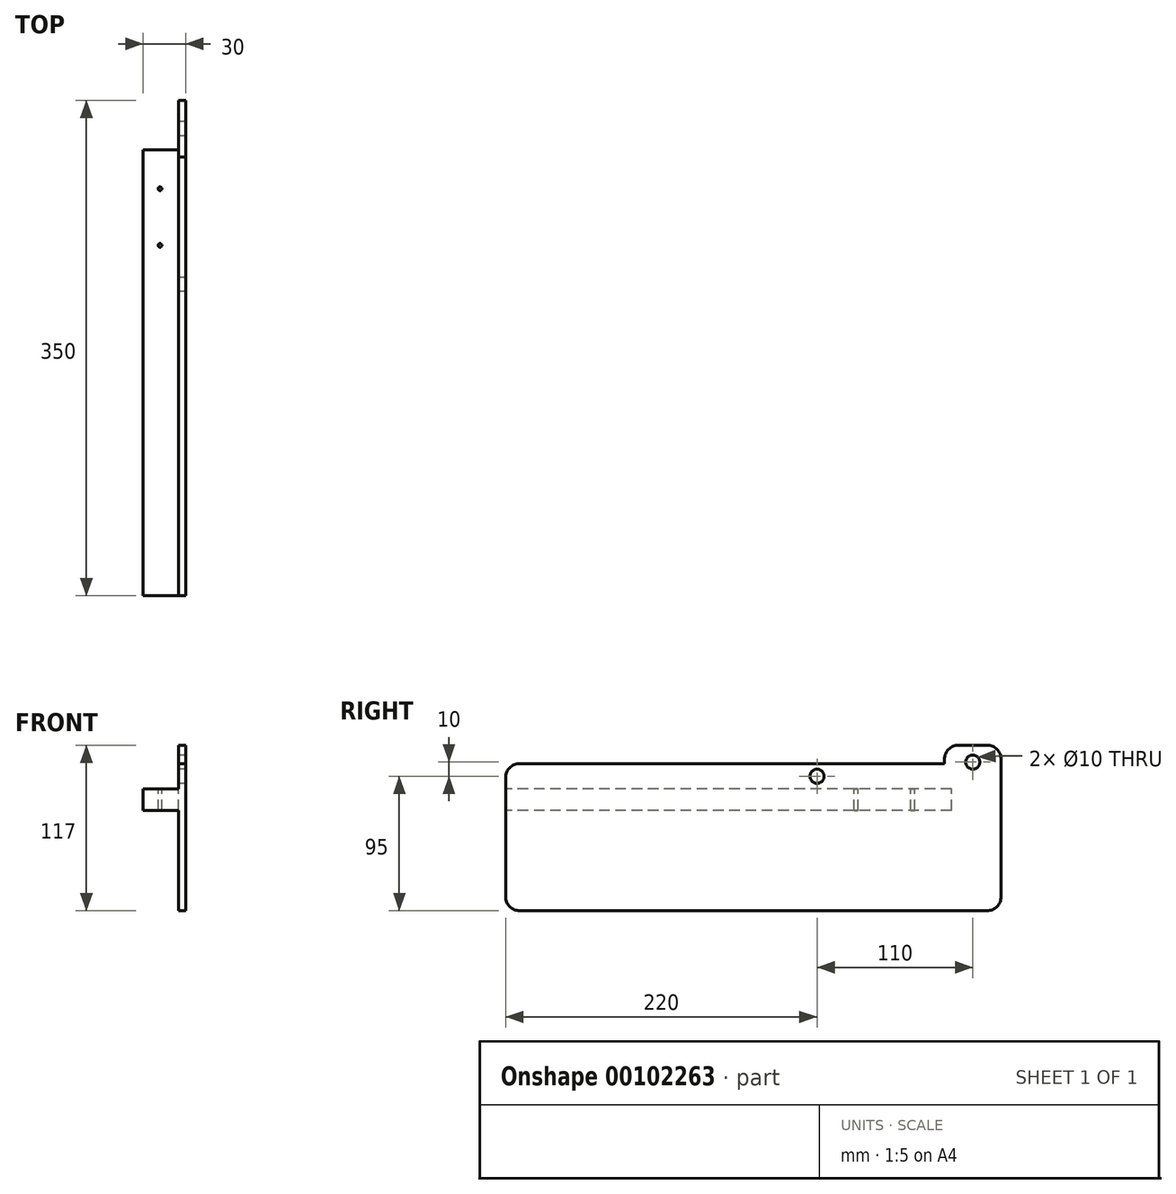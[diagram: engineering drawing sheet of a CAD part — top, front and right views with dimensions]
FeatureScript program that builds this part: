
annotation { "Feature Type Name" : "Feature", "Feature Type Description" : "" }
export const myFeature = defineFeature(function(context is Context, id is Id, definition is map)
    precondition{}
    {
        {
            var Q0;
            Q0=qCreatedBy(makeId("Right.planeOp"),FACE);
            var sketch = newSketch(context, id + "F0", { "sketchPlane" : qUnion([Q0])});
            skLineSegment(sketch, "E0", {"start": v(-320, -1) * mm, "end": v(-20, -1) * mm});
            skLineSegment(sketch, "E1", {"start": v(-20, -1) * mm, "end": v(-20, 2) * mm});
            skLineSegment(sketch, "E2", {"start": v(-10, 12) * mm, "end": v(10, 12) * mm});
            skLineSegment(sketch, "E3", {"start": v(20, 2) * mm, "end": v(20, -95) * mm});
            skLineSegment(sketch, "E4", {"start": v(10, -105) * mm, "end": v(-320, -105) * mm});
            skLineSegment(sketch, "E5", {"start": v(-330, -95) * mm, "end": v(-330, -11) * mm});
            skCircle(sketch, "E6", {"center": v(0, 0) * mm, "radius": 5 * mm});
            skCircle(sketch, "E7", {"center": v(-110, -10) * mm, "radius": 5 * mm});
            skPoint(sketch, "E8.visualSharp", {"position": v(20, -105) * mm});
            skArc(sketch, "E8.filletArc", {"start": v(10, -105) * mm, "mid": v(17.07, -102.07) * mm, "end": v(20, -95) * mm});
            skPoint(sketch, "E9.visualSharp", {"position": v(-330, -105) * mm});
            skArc(sketch, "E9.filletArc", {"start": v(-330, -95) * mm, "mid": v(-327.07, -102.07) * mm, "end": v(-320, -105) * mm});
            skPoint(sketch, "E10.visualSharp", {"position": v(-330, -1) * mm});
            skArc(sketch, "E10.filletArc", {"start": v(-320, -1) * mm, "mid": v(-327.07, -3.93) * mm, "end": v(-330, -11) * mm});
            skPoint(sketch, "E11.visualSharp", {"position": v(-20, 12) * mm});
            skArc(sketch, "E11.filletArc", {"start": v(-10, 12) * mm, "mid": v(-17.07, 9.07) * mm, "end": v(-20, 2) * mm});
            skPoint(sketch, "E12.visualSharp", {"position": v(20, 12) * mm});
            skArc(sketch, "E12.filletArc", {"start": v(20, 2) * mm, "mid": v(17.07, 9.07) * mm, "end": v(10, 12) * mm});
            skSolve(sketch);
        }
        {
            var Q0;
            Q0=makeQuery(id+"F0.imprint","IMPRINT",FACE,{"disambiguationData":[TD([[makeQuery(id+"F0.imprint","IMPRINT",EDGE,{"derivedFrom":sQuery(id+"F0.wireOp",EDGE,"E0")}),-1.0]])]});
            var Q1;
            Q1=qSketchRegion(id+"F0",true);
            extrude(context, id + "F1", {"entities" : qUnion([Q0, Q1]), "depth" : 5 * mm});
        }
        {
            var Q0;
            Q0=makeQuery(id+"F1.opExtrude","CAP_FACE",FACE,{"disambiguationData":[OSD([sQuery(id+"F0.wireOp",EDGE,"E0"),sQuery(id+"F0.wireOp",EDGE,"E1"),sQuery(id+"F0.wireOp",EDGE,"E2"),sQuery(id+"F0.wireOp",EDGE,"E3"),sQuery(id+"F0.wireOp",EDGE,"E4"),sQuery(id+"F0.wireOp",EDGE,"E5"),sQuery(id+"F0.wireOp",EDGE,"E6"),sQuery(id+"F0.wireOp",EDGE,"E7"),sQuery(id+"F0.wireOp",EDGE,"E8.filletArc"),sQuery(id+"F0.wireOp",EDGE,"E9.filletArc"),sQuery(id+"F0.wireOp",EDGE,"E10.filletArc"),sQuery(id+"F0.wireOp",EDGE,"E11.filletArc"),sQuery(id+"F0.wireOp",EDGE,"E12.filletArc")])],"isStart":true});
            var sketch = newSketch(context, id + "F2", { "sketchPlane" : qUnion([Q0])});
            skLineSegment(sketch, "E13.bottom", {"start": v(15, -34) * mm, "end": v(330, -34) * mm});
            skLineSegment(sketch, "E13.top", {"start": v(15, -19) * mm, "end": v(330, -19) * mm});
            skLineSegment(sketch, "E13.left", {"start": v(15, -34) * mm, "end": v(15, -19) * mm});
            skLineSegment(sketch, "E13.right", {"start": v(330, -34) * mm, "end": v(330, -19) * mm});
            skSolve(sketch);
        }
        {
            var Q0;
            Q0=qSketchRegion(id+"F2",true);
            extrude(context, id + "F3", {"entities" : qUnion([Q0]), "operationType" : NewBodyOperationType.ADD, "depth" : 25 * mm});
        }
        {
            var Q0;
            Q0=makeQuery(id+"F3.opExtrude","SWEPT_FACE",FACE,{"disambiguationData":[OSD([sQuery(id+"F2.wireOp",EDGE,"E13.top")])]});
            var sketch = newSketch(context, id + "F4", { "sketchPlane" : qUnion([Q0])});
            skCircle(sketch, "E14", {"center": v(-13, -42.4) * mm, "radius": 3.64 * mm});
            skCircle(sketch, "E15", {"center": v(-13, -82.4) * mm, "radius": 3.2 * mm});
            skLineSegment(sketch, "E16", {"start": v(-13, -82.4) * mm, "end": v(-13, -27.13) * mm, "construction": true});
            skSolve(sketch);
        }
        {
            var Q0;
            Q0=sQuery(id+"F4.wireOp",VERTEX,"E14.center");
            var Q1;
            Q1=sQuery(id+"F4.wireOp",VERTEX,"E15.center");
            var Q2;
            Q2=makeQuery(id+"F1.opExtrude","SWEPT_BODY",BODY,{"disambiguationData":[OSD([sQuery(id+"F0.wireOp",EDGE,"E0"),sQuery(id+"F0.wireOp",EDGE,"E1"),sQuery(id+"F0.wireOp",EDGE,"E2"),sQuery(id+"F0.wireOp",EDGE,"E3"),sQuery(id+"F0.wireOp",EDGE,"E4"),sQuery(id+"F0.wireOp",EDGE,"E5"),sQuery(id+"F0.wireOp",EDGE,"E6"),sQuery(id+"F0.wireOp",EDGE,"E7"),sQuery(id+"F0.wireOp",EDGE,"E8.filletArc"),sQuery(id+"F0.wireOp",EDGE,"E9.filletArc"),sQuery(id+"F0.wireOp",EDGE,"E10.filletArc"),sQuery(id+"F0.wireOp",EDGE,"E11.filletArc"),sQuery(id+"F0.wireOp",EDGE,"E12.filletArc")])]});
            hole(context, id + "F5", {"style" : HoleStyle.SIMPLE, "endStyle" : HoleEndStyle.THROUGH, "holeDiameter" : 2.6 * mm, "locations" : qUnion([Q0, Q1]), "scope" : qUnion([Q2]), "isTappedThrough" : true});
        }
    });
